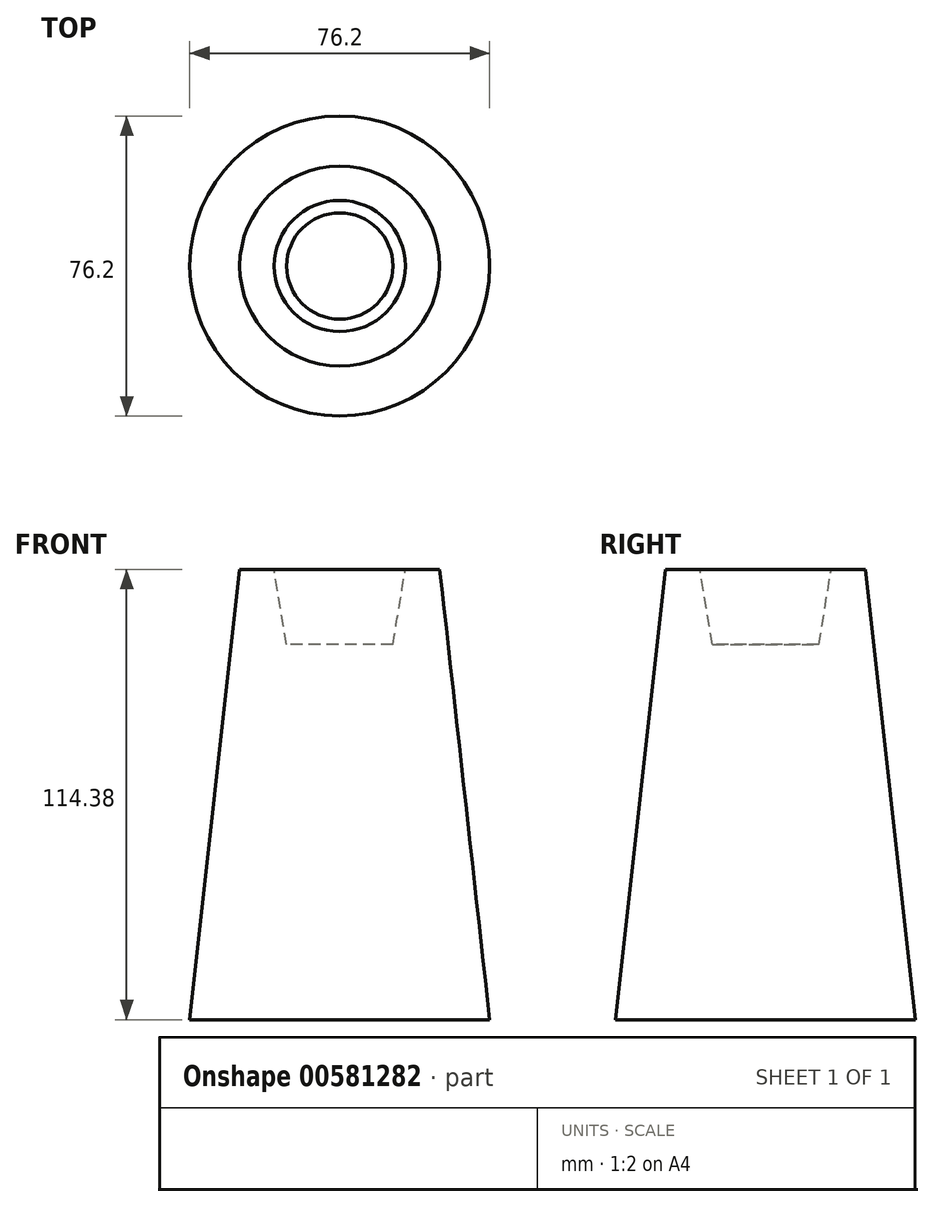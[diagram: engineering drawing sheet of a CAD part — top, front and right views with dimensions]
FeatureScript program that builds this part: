
annotation { "Feature Type Name" : "Feature", "Feature Type Description" : "" }
export const myFeature = defineFeature(function(context is Context, id is Id, definition is map)
    precondition{}
    {
        {
            var Q0;
            Q0=qCreatedBy(makeId("Front.planeOp"),FACE);
            var sketch = newSketch(context, id + "F0", { "sketchPlane" : qUnion([Q0])});
            skLineSegment(sketch, "E0.top", {"start": v(0.04, -57.2) * mm, "end": v(-25.4, -57.2) * mm});
            skPoint(sketch, "E0.middle", {"position": v(-12.66, 0) * mm});
            skLineSegment(sketch, "E1", {"start": v(0.04, 38.14) * mm, "end": v(-13.46, 38.14) * mm});
            skLineSegment(sketch, "E2", {"start": v(-13.46, 38.14) * mm, "end": v(-16.63, 57.2) * mm});
            skLineSegment(sketch, "E3", {"start": v(-25.36, 57.2) * mm, "end": v(-38.06, -57.2) * mm});
            skLineSegment(sketch, "E4", {"start": v(-38.06, -57.2) * mm, "end": v(0.04, -57.2) * mm});
            skLineSegment(sketch, "E5", {"start": v(-16.63, 57.2) * mm, "end": v(-25.36, 57.2) * mm});
            skLineSegment(sketch, "E6", {"start": v(0.04, 38.14) * mm, "end": v(0.04, -57.2) * mm});
            skSolve(sketch);
        }
        {
            var Q0;
            Q0=makeQuery(id+"F0.imprint","IMPRINT",FACE,{"disambiguationData":[TD([[makeQuery(id+"F0.imprint","IMPRINT",EDGE,{"derivedFrom":sQuery(id+"F0.wireOp",EDGE,"E1")}),1.0]])]});
            var Q1;
            Q1=sQuery(id+"F0.wireOp",EDGE,"E6");
            revolve(context, id + "F1", {"entities" : qUnion([Q0]), "axis" : qUnion([Q1]), "revolveType" : RevolveType.FULL});
        }
    });
